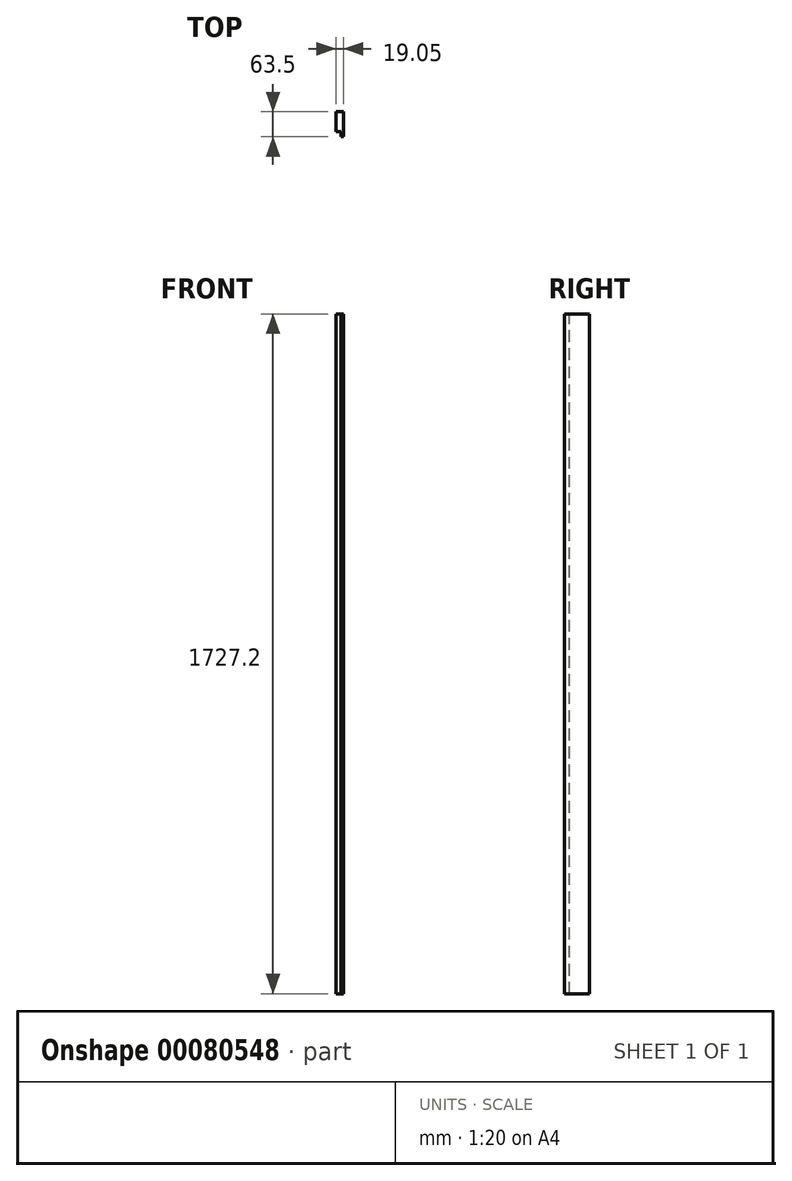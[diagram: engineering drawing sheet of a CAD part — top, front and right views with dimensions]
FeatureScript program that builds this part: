
annotation { "Feature Type Name" : "Feature", "Feature Type Description" : "" }
export const myFeature = defineFeature(function(context is Context, id is Id, definition is map)
    precondition{}
    {
        {
            var Q0;
            Q0=qCreatedBy(makeId("Top.planeOp"),FACE);
            var sketch = newSketch(context, id + "F0", { "sketchPlane" : qUnion([Q0])});
            skLineSegment(sketch, "E0.bottom", {"start": v(142.78, 0) * mm, "end": v(161.83, 0) * mm});
            skLineSegment(sketch, "E0.top", {"start": v(142.78, -63.5) * mm, "end": v(161.83, -63.5) * mm});
            skLineSegment(sketch, "E0.left", {"start": v(142.78, 0) * mm, "end": v(142.78, -63.5) * mm});
            skLineSegment(sketch, "E0.right", {"start": v(161.83, 0) * mm, "end": v(161.83, -63.5) * mm});
            skSolve(sketch);
        }
        {
            var Q0;
            Q0 = qSketchRegion(id + "F0", true);
            extrude(context, id + "F1", {"entities" : qUnion([Q0]), "depth" : 1727.2 * mm});
        }
        {
            var Q0;
            Q0=makeQuery(id+"F1.opExtrude","CAP_FACE",FACE,{"disambiguationData":[OSD([sQuery(id+"F0.wireOp",EDGE,"E0.bottom"),sQuery(id+"F0.wireOp",EDGE,"E0.top"),sQuery(id+"F0.wireOp",EDGE,"E0.left"),sQuery(id+"F0.wireOp",EDGE,"E0.right")])],"isStart":false});
            var sketch = newSketch(context, id + "F2", { "sketchPlane" : qUnion([Q0])});
            skLineSegment(sketch, "E1", {"start": v(155.48, -63.5) * mm, "end": v(155.48, -50.8) * mm});
            skLineSegment(sketch, "E2", {"start": v(155.48, -50.8) * mm, "end": v(142.78, -50.8) * mm});
            skSolve(sketch);
        }
        {
            var Q0;
            Q0 = qSketchRegion(id + "F2", true);
            var Q1;
            {var subQ0=sQuery(id+"F2.wireOp",EDGE,"E1");Q1=makeQuery(id+"F2.imprint","IMPRINT",FACE,{"disambiguationData":[TD([[makeQuery(id+"F2.imprint","IMPRINT",EDGE,{"derivedFrom":subQ0}),1.0]])]});}
            extrude(context, id + "F3", {"entities" : qUnion([Q0, Q1]), "operationType" : NewBodyOperationType.REMOVE, "endBound" : BoundingType.THROUGH_ALL, "oppositeDirection" : true, "depth" : 25.4 * mm});
        }
    });
